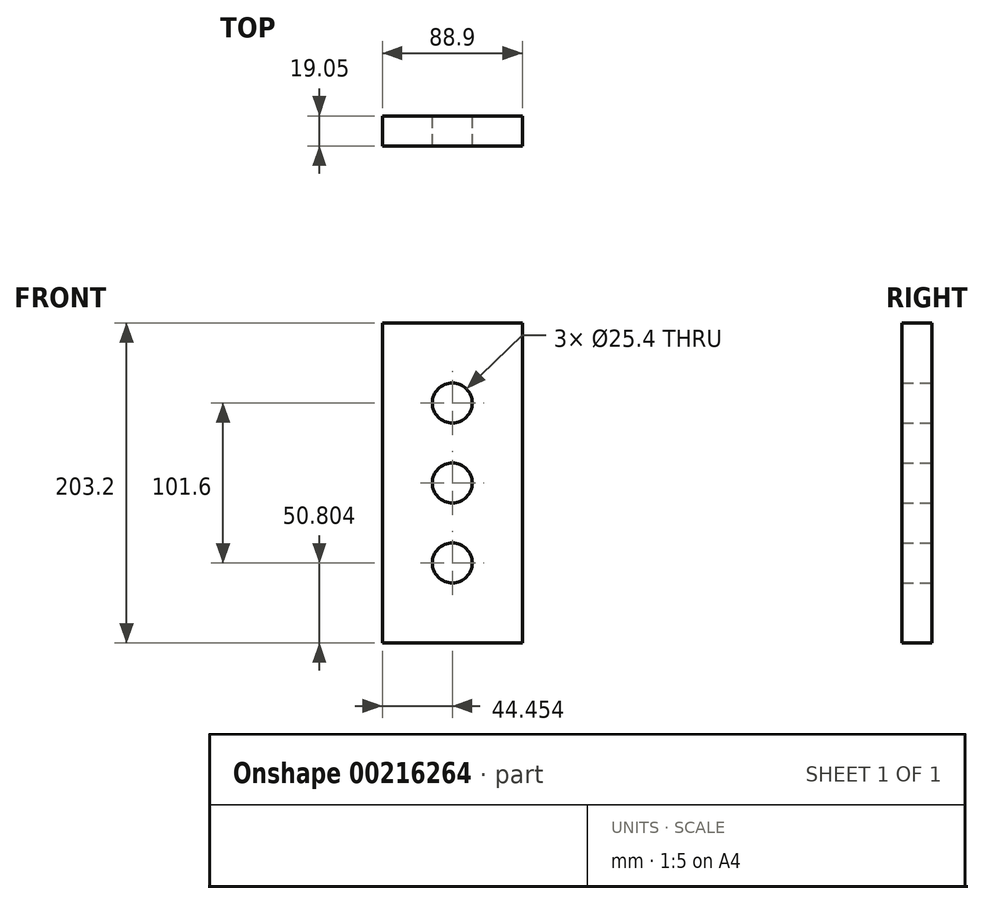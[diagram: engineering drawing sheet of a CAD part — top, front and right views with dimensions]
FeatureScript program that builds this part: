
annotation { "Feature Type Name" : "Feature", "Feature Type Description" : "" }
export const myFeature = defineFeature(function(context is Context, id is Id, definition is map)
    precondition{}
    {
        {
            var Q0;
            Q0=qCreatedBy(makeId("Front.planeOp"),FACE);
            var sketch = newSketch(context, id + "F0", { "sketchPlane" : qUnion([Q0])});
            skLineSegment(sketch, "E0", {"start": v(-4102.78, -1606) * mm, "end": v(-4013.88, -1606) * mm});
            skLineSegment(sketch, "E1", {"start": v(-4013.88, -1606) * mm, "end": v(-4013.88, -1402.8) * mm});
            skLineSegment(sketch, "E2", {"start": v(-4013.88, -1402.8) * mm, "end": v(-4102.78, -1402.8) * mm});
            skLineSegment(sketch, "E3", {"start": v(-4102.78, -1402.8) * mm, "end": v(-4102.78, -1606) * mm});
            skCircle(sketch, "E4", {"center": v(-4058.33, -1504.4) * mm, "radius": 12.7 * mm});
            skCircle(sketch, "E5", {"center": v(-4058.33, -1453.6) * mm, "radius": 12.7 * mm});
            skCircle(sketch, "E6", {"center": v(-4058.33, -1555.2) * mm, "radius": 12.7 * mm});
            skLineSegment(sketch, "E7", {"start": v(-4058.33, -1606) * mm, "end": v(-4058.33, -1402.8) * mm, "construction": true});
            skSolve(sketch);
        }
        {
            var Q0;
            Q0=makeQuery(id+"F0.imprint","IMPRINT",FACE,{"disambiguationData":[TD([[makeQuery(id+"F0.imprint","IMPRINT",EDGE,{"derivedFrom":sQuery(id+"F0.wireOp",EDGE,"E0")}),1.0]])]});
            extrude(context, id + "F1", {"entities" : qUnion([Q0]), "depth" : 19.05 * mm});
        }
    });
